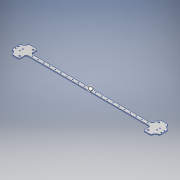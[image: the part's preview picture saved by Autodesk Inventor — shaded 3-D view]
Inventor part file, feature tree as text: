
AUTODESK INVENTOR PART (.ipt)
format: ipt  version: 2019 (Build 230136000, 136)  size: 339,968 bytes
history: native  units: mm
features: sketch x5, other x4, extrude x2, thicken_offset x2, sheet_metal_op x1, mirror x1, hole x1, pattern_linear x1, chamfer x1
ambient origin geometry x8: Origin, YZ Plane, XZ Plane, XY Plane, X Axis, Y Axis, Z Axis, Center Point
bodies: Solid1 (feature_tree)
feature tree (18):
  sheet_metal_op  "Face1"
  extrude  "Extrusion1"  Depth=11.0mm
  extrude  "Extrusion2"  Depth=41.0mm
  mirror  "Mirror2"
  thicken_offset  "Thicken1"
  thicken_offset  "Thicken3"
  hole  "Hole1"  [1 undecoded]
  pattern_linear  "Rectangular Pattern1"  Spacing1=15.0mm  [1 undecoded]
  chamfer  "Corner Round1"
  sketch  "Sketch1"  dims[d0=11.0mm d1=215.0mm]
  other  "Plate1"
  sketch  "Sketch2"  dims[d2=60.0mm d3=41.0mm]
  sketch  "Sketch3"  dims[d4=0.8mm d5=30.0mm]
  sketch  "Sketch4"  dims[d6=10.0mm d7=0.0mm]
  sketch  "Sketch6"  dims[d10=3.5mm d11=15.0mm d12=10.0mm d13=3.2mm d14=10.0mm d15=0.0mm d18=2.5mm d21=210.0mm d23=20.0mm d26=5.2mm d27=3.0mm d28=0.0mm d32=3.0mm d33=5.0mm d34=5.0mm d37=5.2mm d38=3.0mm d39=0.0mm d42=9.0mm d45=7.5mm d47=9.0mm d49=7.5mm d50=9.0mm d51=7.5mm d52=9.0mm d53=6.0mm d54=5.0mm d55=5.0mm d56=7.5mm d57=2.459mm d58=6.0mm d59=3.023mm d60=2.0mm d61=14.3117mm d62=8.8mm d63=20.594885mm d64=0.0mm d65=0.0mm]
  other  "Cut2"
  other  "Cut3"
  other  "Definition1"
note: 2 required parameter values undecoded (feature->parameter linkage not recoverable at this tier; creation-order binding heuristic only, values carry confidence <= 0.55)
